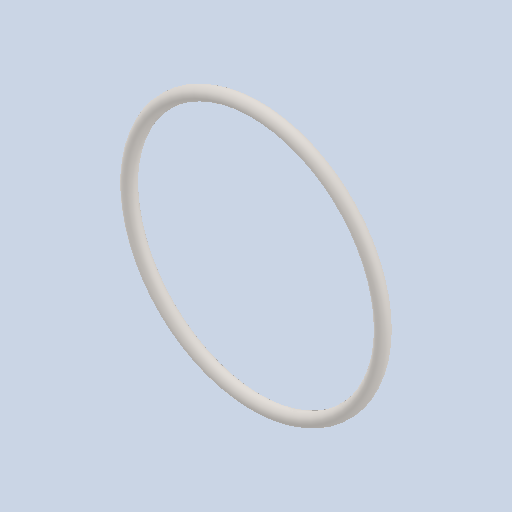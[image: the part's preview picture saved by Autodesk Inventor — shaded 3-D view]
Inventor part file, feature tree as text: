
AUTODESK INVENTOR PART (.ipt)
format: ipt  version: 2024.1 (Build 281209000, 209)  size: 112,128 bytes
history: native  units: in
note: dims shown in document units (in); Inventor stores cm internally (conversion verified against a paired STEP export)
features: sweep x1
ambient origin geometry x8: Origin, YZ Plane, XZ Plane, XY Plane, X Axis, Y Axis, Z Axis, Center Point
bodies: Solid1 (feature_tree)
feature tree (1):
  sweep  "Sweep1"
